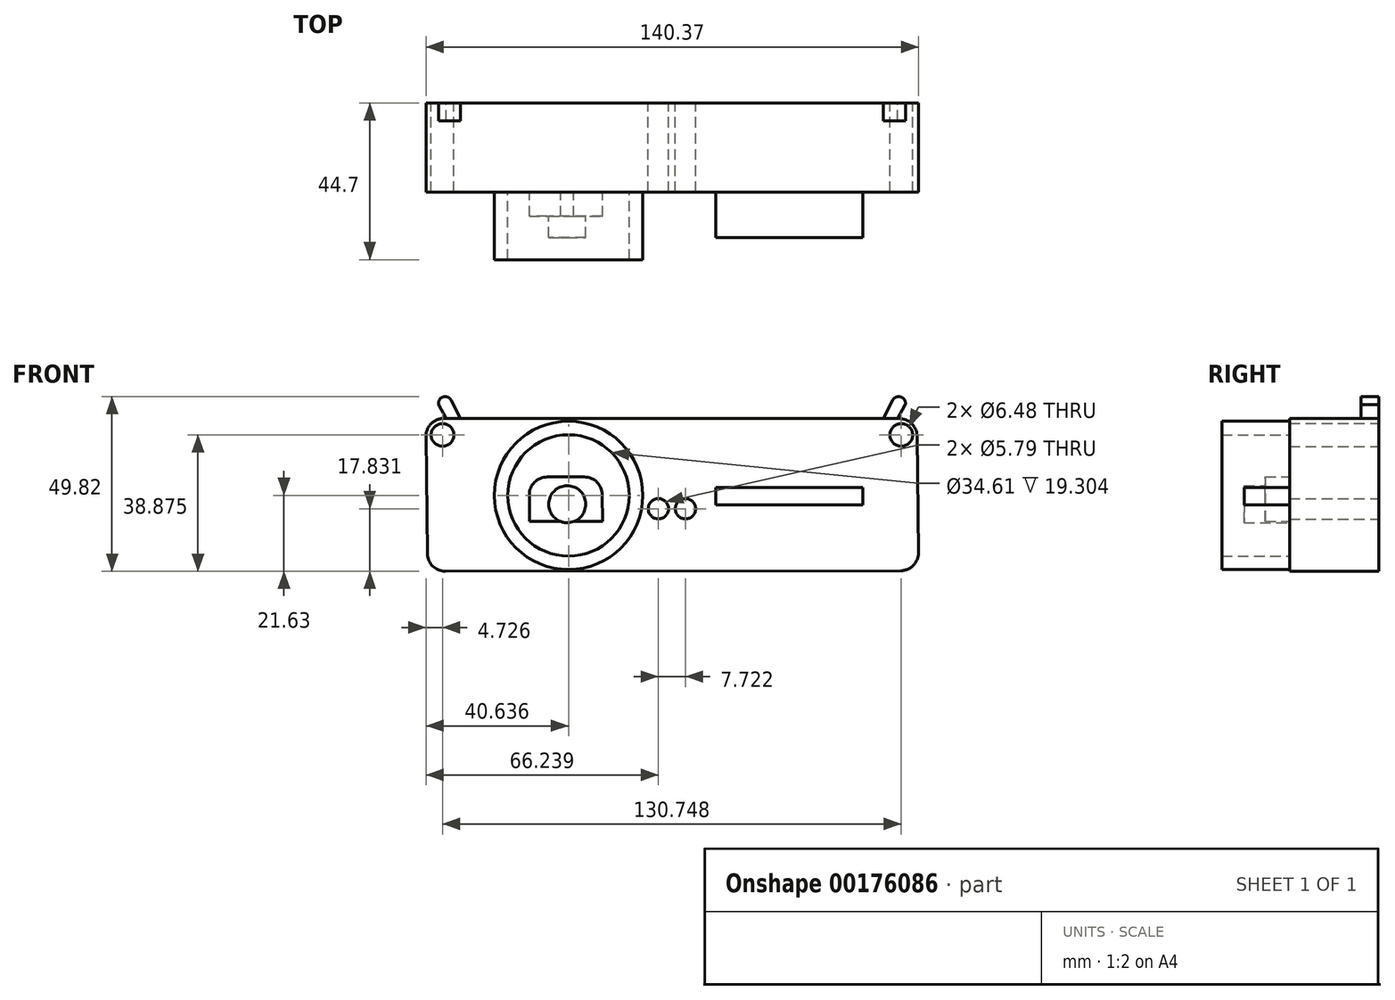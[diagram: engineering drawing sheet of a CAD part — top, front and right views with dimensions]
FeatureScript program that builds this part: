
annotation { "Feature Type Name" : "Feature", "Feature Type Description" : "" }
export const myFeature = defineFeature(function(context is Context, id is Id, definition is map)
    precondition{}
    {
        {
            var Q0;
            Q0=qCreatedBy(makeId("Front.planeOp"),FACE);
            var sketch = newSketch(context, id + "F0", { "sketchPlane" : qUnion([Q0])});
            skLineSegment(sketch, "E0", {"start": v(69.76, 21.97) * mm, "end": v(-70.17, 21.97) * mm});
            skLineSegment(sketch, "E1", {"start": v(69.76, 21.97) * mm, "end": v(70.34, -21.45) * mm});
            skLineSegment(sketch, "E2", {"start": v(70.34, -21.45) * mm, "end": v(-69.6, -21.64) * mm});
            skLineSegment(sketch, "E3", {"start": v(-69.6, -21.64) * mm, "end": v(-70.17, 21.97) * mm});
            skCircle(sketch, "E4", {"center": v(-65.37, 17.25) * mm, "radius": 3.24 * mm});
            skCircle(sketch, "E5", {"center": v(-3.86, -3.8) * mm, "radius": 2.9 * mm});
            skCircle(sketch, "E6.MirrorC", {"center": v(65.37, 17.25) * mm, "radius": 3.24 * mm});
            skCircle(sketch, "E7.MirrorC", {"center": v(3.86, -3.8) * mm, "radius": 2.9 * mm});
            skLineSegment(sketch, "E8", {"start": v(-64.28, 21.97) * mm, "end": v(-66.52, 25.94) * mm});
            skLineSegment(sketch, "E9", {"start": v(-62.9, 27.14) * mm, "end": v(-60.25, 21.97) * mm});
            skLineSegment(sketch, "E10.MirrorCS", {"start": v(62.9, 27.14) * mm, "end": v(60.25, 21.97) * mm});
            skLineSegment(sketch, "E11.MirrorCS", {"start": v(64.28, 21.97) * mm, "end": v(66.52, 25.94) * mm});
            skArc(sketch, "E12", {"start": v(66.52, 25.94) * mm, "mid": v(65.22, 28.09) * mm, "end": v(62.9, 27.14) * mm});
            skArc(sketch, "E13", {"start": v(-62.9, 27.14) * mm, "mid": v(-65.22, 28.09) * mm, "end": v(-66.52, 25.94) * mm});
            skSolve(sketch);
        }
        {
            var Q0;
            Q0=makeQuery(id+"F0.imprint","IMPRINT",FACE,{"disambiguationData":[TD([[makeQuery(id+"F0.imprint","IMPRINT",EDGE,{"derivedFrom":sQuery(id+"F0.wireOp",EDGE,"E0")}),1.0]])]});
            extrude(context, id + "F1", {"entities" : qUnion([Q0]), "depth" : 25.4 * mm});
        }
        {
            var Q0;
            Q0=makeQuery(id+"F1.opExtrude","SWEPT_EDGE",EDGE,{"disambiguationData":[OSD([sQuery(id+"F0.wireOp",EDGE,"E0"),sQuery(id+"F0.wireOp",EDGE,"E1")])]});
            var Q1;
            Q1=makeQuery(id+"F1.opExtrude","SWEPT_EDGE",EDGE,{"disambiguationData":[OSD([sQuery(id+"F0.wireOp",EDGE,"E0"),sQuery(id+"F0.wireOp",EDGE,"E3")])]});
            var Q2;
            Q2=makeQuery(id+"F1.opExtrude","SWEPT_EDGE",EDGE,{"disambiguationData":[OSD([sQuery(id+"F0.wireOp",EDGE,"E2"),sQuery(id+"F0.wireOp",EDGE,"E3")])]});
            var Q3;
            Q3=makeQuery(id+"F1.opExtrude","SWEPT_EDGE",EDGE,{"disambiguationData":[OSD([sQuery(id+"F0.wireOp",EDGE,"E1"),sQuery(id+"F0.wireOp",EDGE,"E2")])]});
            fillet(context, id + "F2", {"entities" : qUnion([Q0, Q1, Q2, Q3]), "radius" : 5.08 * mm, "tangentPropagation" : true, "allowEdgeOverflow" : false});
        }
        {
            var Q0;
            {var subQ0=sQuery(id+"F0.wireOp",EDGE,"E8");Q0=makeQuery(id+"F0.imprint","IMPRINT",FACE,{"disambiguationData":[TD([[makeQuery(id+"F0.imprint","IMPRINT",EDGE,{"derivedFrom":subQ0}),-1.0]])]});}
            var Q1;
            {var subQ0=sQuery(id+"F0.wireOp",EDGE,"E10.MirrorCS");Q1=makeQuery(id+"F0.imprint","IMPRINT",FACE,{"disambiguationData":[TD([[makeQuery(id+"F0.imprint","IMPRINT",EDGE,{"derivedFrom":subQ0}),1.0]])]});}
            extrude(context, id + "F3", {"entities" : qUnion([Q0, Q1]), "operationType" : NewBodyOperationType.ADD, "depth" : 5.08 * mm});
        }
        {
            var Q0;
            Q0=qCreatedBy(makeId("Front.planeOp"),FACE);
            var sketch = newSketch(context, id + "F4", { "sketchPlane" : qUnion([Q0])});
            skLineSegment(sketch, "E14.top", {"start": v(-40.63, 5.26) * mm, "end": v(-19.9, 5.26) * mm});
            skLineSegment(sketch, "E15", {"start": v(-40.63, -7.44) * mm, "end": v(-19.8, -7.44) * mm});
            skLineSegment(sketch, "E16", {"start": v(-40.63, 5.26) * mm, "end": v(-40.63, -7.44) * mm});
            skLineSegment(sketch, "E17", {"start": v(-19.9, 5.26) * mm, "end": v(-19.8, -7.44) * mm});
            skSolve(sketch);
        }
        {
            var Q0;
            Q0 = qSketchRegion(id + "F4", true);
            extrude(context, id + "F5", {"entities" : qUnion([Q0]), "operationType" : NewBodyOperationType.ADD, "depth" : 32.33 * mm});
        }
        {
            var Q0;
            Q0=makeQuery(id+"F5.opExtrude","SWEPT_EDGE",EDGE,{"disambiguationData":[OSD([sQuery(id+"F4.wireOp",EDGE,"E14.top"),sQuery(id+"F4.wireOp",EDGE,"E16")])]});
            var Q1;
            Q1=makeQuery(id+"F5.opExtrude","SWEPT_EDGE",EDGE,{"disambiguationData":[OSD([sQuery(id+"F4.wireOp",EDGE,"E14.top"),sQuery(id+"F4.wireOp",EDGE,"E17")])]});
            fillet(context, id + "F6", {"entities" : qUnion([Q0, Q1]), "radius" : 5.08 * mm, "tangentPropagation" : true, "allowEdgeOverflow" : false});
        }
        {
            var Q0;
            Q0=qCreatedBy(makeId("Front.planeOp"),FACE);
            var sketch = newSketch(context, id + "F7", { "sketchPlane" : qUnion([Q0])});
            skCircle(sketch, "E18", {"center": v(-29.85, -2.5) * mm, "radius": 5.28 * mm});
            skSolve(sketch);
        }
        {
            var Q0;
            Q0 = qSketchRegion(id + "F7", true);
            extrude(context, id + "F8", {"entities" : qUnion([Q0]), "operationType" : NewBodyOperationType.ADD, "depth" : 38.35 * mm});
        }
        {
            var Q0;
            Q0=qCreatedBy(makeId("Front.planeOp"),FACE);
            var sketch = newSketch(context, id + "F9", { "sketchPlane" : qUnion([Q0])});
            skCircle(sketch, "E19", {"center": v(-29.46, 0) * mm, "radius": 21.16 * mm});
            skCircle(sketch, "E20", {"center": v(-29.46, 0) * mm, "radius": 17.3 * mm});
            skSolve(sketch);
        }
        {
            var Q0;
            Q0 = qSketchRegion(id + "F9", true);
            extrude(context, id + "F10", {"entities" : qUnion([Q0]), "operationType" : NewBodyOperationType.ADD, "depth" : 44.7 * mm});
        }
        {
            var Q0;
            Q0=qCreatedBy(makeId("Front.planeOp"),FACE);
            var sketch = newSketch(context, id + "F11", { "sketchPlane" : qUnion([Q0])});
            skLineSegment(sketch, "E21", {"start": v(12.47, 2.22) * mm, "end": v(54.37, 2.22) * mm});
            skLineSegment(sketch, "E22", {"start": v(54.37, 2.22) * mm, "end": v(54.37, -2.63) * mm});
            skLineSegment(sketch, "E23", {"start": v(54.37, -2.63) * mm, "end": v(12.48, -2.63) * mm});
            skLineSegment(sketch, "E24", {"start": v(12.48, -2.63) * mm, "end": v(12.47, 2.22) * mm});
            skSolve(sketch);
        }
        {
            var Q0;
            Q0 = qSketchRegion(id + "F11", true);
            extrude(context, id + "F12", {"entities" : qUnion([Q0]), "operationType" : NewBodyOperationType.ADD, "depth" : 38.35 * mm});
        }
    });
